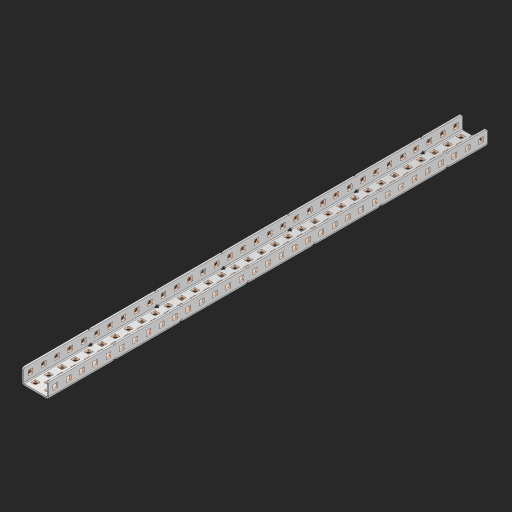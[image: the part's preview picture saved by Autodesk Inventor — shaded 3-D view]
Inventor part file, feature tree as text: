
AUTODESK INVENTOR PART (.ipt)
format: ipt  version: 2023 (Build 270158000, 158)  size: 2,024,960 bytes
history: native  units: in
note: dims shown in document units (in); Inventor stores cm internally (conversion verified against a paired STEP export)
features: other x172, extrude x163, sheet_metal_op x11, sketch x10, pattern_linear x2, mirror x1, chamfer x1
ambient origin geometry x8: Origin, YZ Plane, XZ Plane, XY Plane, X Axis, Y Axis, Z Axis, Center Point
bodies: Solid1 (feature_tree), Body (feature_tree)
feature tree (360):
  sheet_metal_op  "Flanges"
  other  "Flange Pattern Plane"
  other  "Flange Pattern Sketch"
  sheet_metal_op  "Flange Pattern"
  sheet_metal_op  "Body Pattern"
  pattern_linear  "Center Pattern"  Spacing1=0.0625in  [1 undecoded]
  other  "Arc Length"
  mirror  "Notch Mirror"
  pattern_linear  "Notch Pattern"  Spacing1=0.182in  [1 undecoded]
  chamfer  "End Chamfer"
  extrude  "Half Cut"  Depth=0.02in
  sketch  "Sketch1"  dims[d0=1.0in]
  other  "Plate1"
  sketch  "Sketch2"  dims[d1=16.5in]
  other  "Plate2"
  sheet_metal_op  "Bend1"
  sheet_metal_op  "Corner1"
  sketch  "Sketch3"  dims[d2=0.0625in]
  sketch  "Sketch7"  dims[d3=0.0625in]
  other  "Srf1"
  other  "Srf2"
  sketch  "Sketch8"  dims[d4=0.0312in]
  sketch  "Sketch9"  dims[d5=0.125in]
  other  "Srf91"
  sheet_metal_op  "Body Pattern Sketch"
  other  "Srf92"
  sketch  "Sketch13"  dims[d6=0.0625in]
  sketch  "Sketch14"  dims[d7=0.5in d8=90.0deg d9=0.0312in]
  sketch  "Sketch15"  dims[d10=0.25in]
  sketch  "Sketch16"  dims[d11=0.0625in d12=0.0625in d16=0.182in d17=0.02in d18=0.0625in d19=0.0in d20=0.25in d21=0.25in d38=12.9921in d40=0.5in d41=0.7874in d43=1.0in d46=0.172in d47=1.0in d48=0.0in d49=0.182in d50=0.02in d51=0.25in d52=0.25in d53=0.0625in d54=0.0in d55=0.172in d56=1.0in d57=0.0in d58=0.25in d60=12.9921in d62=0.5in d63=0.7874in d65=0.5in d85=0.1473in d86=0.1782in d88=0.04in d89=0.0625in d90=0.0in d91=0.04in d92=0.0491in d95=2.5in d96=0.04in d97=0.25in d98=45.0deg d99=0.25in d100=0.5in d101=0.0in d102=2.497in d106=0.182in d107=0.02in d108=0.5in d109=0.5in d110=0.0625in d111=0.0in d112=0.172in d113=0.5in d114=0.0in d117=0.5in d118=0.5in d119=0.5in]
  other  "Srf786"
  other  "Srf823"
  other  "Srf824"
  other  "Srf825"
  other  "Srf826"
  other  "Srf827"
  other  "Srf828"
  other  "Srf829"
  other  "Srf856"
  other  "Srf857"
  other  "Srf858"
  other  "Srf859"
  other  "Srf860"
  other  "Srf861"
  other  "Srf862"
  other  "Srf889"
  other  "Srf890"
  other  "Srf891"
  other  "Srf892"
  other  "Srf893"
  other  "Srf894"
  other  "Srf895"
  other  "Srf896"
  other  "Srf922"
  other  "Srf923"
  other  "Srf924"
  other  "Srf925"
  other  "Srf926"
  other  "Srf959"
  other  "Srf960"
  other  "Srf961"
  other  "Srf962"
  other  "Srf963"
  other  "Srf996"
  other  "Srf997"
  other  "Srf998"
  other  "Srf999"
  other  "Srf1000"
  other  "Srf1143"
  other  "Srf1144"
  other  "Srf1145"
  other  "Srf1146"
  other  "Srf1147"
  other  "Srf1148"
  other  "Srf1149"
  other  "Srf1150"
  other  "Srf1151"
  other  "Srf1152"
  other  "Srf1153"
  other  "Srf1154"
  other  "Srf1155"
  other  "Srf1156"
  other  "Srf1157"
  other  "Srf1158"
  other  "Srf1159"
  other  "Srf1160"
  other  "Srf1161"
  other  "Srf1162"
  other  "Srf1163"
  other  "Srf1164"
  other  "Srf1165"
  other  "Srf1166"
  other  "Srf1167"
  other  "Srf1168"
  other  "Srf1169"
  other  "Srf1170"
  other  "Srf1171"
  other  "Srf1172"
  other  "Srf1173"
  other  "Srf1174"
  other  "Srf1175"
  other  "Srf1176"
  other  "Srf1177"
  other  "Srf1178"
  other  "Srf1179"
  other  "Srf1180"
  other  "Srf1181"
  other  "Srf1182"
  other  "Srf1183"
  other  "Srf1184"
  other  "Srf1185"
  other  "Srf1186"
  other  "Srf1187"
  other  "Srf1188"
  other  "Srf1189"
  other  "Srf1190"
  other  "Srf1191"
  other  "Srf1192"
  other  "Srf1193"
  other  "Srf1194"
  other  "Srf1199"
  other  "Srf1200"
  other  "Srf1201"
  other  "Srf1202"
  other  "Srf1203"
  other  "Srf1204"
  other  "Srf1205"
  other  "Srf1206"
  other  "Srf1207"
  other  "Srf1208"
  other  "Srf1209"
  other  "Srf1210"
  other  "Srf1211"
  other  "Srf1212"
  other  "Srf1213"
  other  "Srf1214"
  other  "Srf1215"
  other  "Srf1216"
  other  "Srf1217"
  other  "Srf1218"
  other  "Srf1219"
  other  "Srf1220"
  other  "Srf1221"
  other  "Srf1222"
  other  "Srf1223"
  other  "Srf1224"
  other  "Srf1225"
  other  "Srf1226"
  other  "Srf1227"
  other  "Srf1228"
  other  "Srf1229"
  other  "Srf1230"
  other  "Srf1231"
  other  "Srf1232"
  other  "Srf1233"
  other  "Srf1234"
  other  "Srf1235"
  other  "Srf1236"
  other  "Srf1237"
  other  "Srf1238"
  other  "Srf1239"
  other  "Srf1240"
  other  "Srf1241"
  other  "Srf1242"
  other  "Srf1243"
  other  "Srf1244"
  other  "Srf1245"
  other  "Srf1246"
  other  "Srf1247"
  other  "Srf1248"
  other  "Srf1249"
  other  "Srf1250"
  other  "Srf1255"
  other  "Srf1256"
  other  "Srf1257"
  other  "Srf1258"
  other  "Srf1259"
  other  "Srf1260"
  other  "Srf1261"
  other  "Srf1262"
  other  "Srf1263"
  other  "Srf1264"
  other  "Srf1265"
  other  "Srf1266"
  other  "Srf1267"
  other  "Srf1268"
  other  "Srf1269"
  other  "Srf1270"
  other  "Srf1271"
  other  "Srf1272"
  other  "Srf1273"
  sheet_metal_op  "Flange Stamp"
  sheet_metal_op  "Flange Circle"
  sheet_metal_op  "Body Stamp"
  sheet_metal_op  "Body Circle"
  other  "Center Stamp"
  other  "Center Circle"
  sheet_metal_op  "Notch"
  extrude  "ExtrusionSrf2"  Depth=0.0625in
  extrude  "ExtrusionSrf92"  TaperAngle=0.0deg  [1 undecoded]
  extrude  "ExtrusionSrf823"  Depth=0.5in
  extrude  "ExtrusionSrf824"  Depth=0.5in
  extrude  "ExtrusionSrf825"  Depth=0.5in
  extrude  "ExtrusionSrf826"  Depth=0.5in
  extrude  "ExtrusionSrf827"  Depth=1.0in TaperAngle=0.0deg
  extrude  "ExtrusionSrf828"  Depth=0.5in
  extrude  "ExtrusionSrf829"  Depth=0.02in
  extrude  "ExtrusionSrf856"  Depth=0.5in
  extrude  "ExtrusionSrf857"  Depth=0.5in
  extrude  "ExtrusionSrf858"  Depth=0.0625in
  extrude  "ExtrusionSrf859"  TaperAngle=0.0deg  [1 undecoded]
  extrude  "ExtrusionSrf860"  Depth=0.5in
  extrude  "ExtrusionSrf861"  Depth=1.0in TaperAngle=0.0deg
  extrude  "ExtrusionSrf862"  Depth=0.5in
  extrude  "ExtrusionSrf889"  Depth=0.5in
  extrude  "ExtrusionSrf890"  Depth=0.5in
  extrude  "ExtrusionSrf891"  Depth=0.5in
  extrude  "ExtrusionSrf892"  Depth=0.5in
  extrude  "ExtrusionSrf893"  Depth=0.5in
  extrude  "ExtrusionSrf894"  Depth=0.0625in
  extrude  "ExtrusionSrf895"  TaperAngle=0.0deg  [1 undecoded]
  extrude  "ExtrusionSrf896"  Depth=0.5in
  extrude  "ExtrusionSrf922"  Depth=0.5in
  extrude  "ExtrusionSrf923"  Depth=2.5in
  extrude  "ExtrusionSrf924"  Depth=0.5in TaperAngle=45.0deg
  extrude  "ExtrusionSrf925"  Depth=0.5in
  extrude  "ExtrusionSrf926"  Depth=0.5in TaperAngle=0.0deg
  extrude  "ExtrusionSrf959"  Depth=0.5in
  extrude  "ExtrusionSrf960"  Depth=0.5in
  extrude  "ExtrusionSrf961"  Depth=0.02in
  extrude  "ExtrusionSrf962"  Depth=0.5in
  extrude  "ExtrusionSrf963"  Depth=0.5in
  extrude  "ExtrusionSrf996"  Depth=0.0625in
  extrude  "ExtrusionSrf997"  TaperAngle=0.0deg  [1 undecoded]
  extrude  "ExtrusionSrf998"  Depth=0.5in
  extrude  "ExtrusionSrf999"  Depth=0.5in TaperAngle=0.0deg
  extrude  "ExtrusionSrf1000"  Depth=0.5in
  extrude  "ExtrusionSrf1143"  Depth=0.5in
  extrude  "ExtrusionSrf1144"  Depth=0.5in
  extrude  "ExtrusionSrf1145"  [1 undecoded]
  extrude  "ExtrusionSrf1146"  [1 undecoded]
  extrude  "ExtrusionSrf1147"  [1 undecoded]
  extrude  "ExtrusionSrf1148"  [1 undecoded]
  extrude  "ExtrusionSrf1149"  [1 undecoded]
  extrude  "ExtrusionSrf1150"  [1 undecoded]
  extrude  "ExtrusionSrf1151"  [1 undecoded]
  extrude  "ExtrusionSrf1152"  [1 undecoded]
  extrude  "ExtrusionSrf1153"  [1 undecoded]
  extrude  "ExtrusionSrf1154"  [1 undecoded]
  extrude  "ExtrusionSrf1155"  [1 undecoded]
  extrude  "ExtrusionSrf1156"  [1 undecoded]
  extrude  "ExtrusionSrf1157"  [1 undecoded]
  extrude  "ExtrusionSrf1158"  [1 undecoded]
  extrude  "ExtrusionSrf1159"  [1 undecoded]
  extrude  "ExtrusionSrf1160"  [1 undecoded]
  extrude  "ExtrusionSrf1161"  [1 undecoded]
  extrude  "ExtrusionSrf1162"  [1 undecoded]
  extrude  "ExtrusionSrf1163"  [1 undecoded]
  extrude  "ExtrusionSrf1164"  [1 undecoded]
  extrude  "ExtrusionSrf1165"  [1 undecoded]
  extrude  "ExtrusionSrf1166"  [1 undecoded]
  extrude  "ExtrusionSrf1167"  [1 undecoded]
  extrude  "ExtrusionSrf1168"  [1 undecoded]
  extrude  "ExtrusionSrf1169"  [1 undecoded]
  extrude  "ExtrusionSrf1170"  [1 undecoded]
  extrude  "ExtrusionSrf1171"  [1 undecoded]
  extrude  "ExtrusionSrf1172"  [1 undecoded]
  extrude  "ExtrusionSrf1173"  [1 undecoded]
  extrude  "ExtrusionSrf1174"  [1 undecoded]
  extrude  "ExtrusionSrf1175"  [1 undecoded]
  extrude  "ExtrusionSrf1176"  [1 undecoded]
  extrude  "ExtrusionSrf1177"  [1 undecoded]
  extrude  "ExtrusionSrf1178"  [1 undecoded]
  extrude  "ExtrusionSrf1179"  [1 undecoded]
  extrude  "ExtrusionSrf1180"  [1 undecoded]
  extrude  "ExtrusionSrf1181"  [1 undecoded]
  extrude  "ExtrusionSrf1182"  [1 undecoded]
  extrude  "ExtrusionSrf1183"  [1 undecoded]
  extrude  "ExtrusionSrf1184"  [1 undecoded]
  extrude  "ExtrusionSrf1185"  [1 undecoded]
  extrude  "ExtrusionSrf1186"  [1 undecoded]
  extrude  "ExtrusionSrf1187"  [1 undecoded]
  extrude  "ExtrusionSrf1188"  [1 undecoded]
  extrude  "ExtrusionSrf1189"  [1 undecoded]
  extrude  "ExtrusionSrf1190"  [1 undecoded]
  extrude  "ExtrusionSrf1191"  [1 undecoded]
  extrude  "ExtrusionSrf1192"  [1 undecoded]
  extrude  "ExtrusionSrf1193"  [1 undecoded]
  extrude  "ExtrusionSrf1194"  [1 undecoded]
  extrude  "ExtrusionSrf1199"  [1 undecoded]
  extrude  "ExtrusionSrf1200"  [1 undecoded]
  extrude  "ExtrusionSrf1201"  [1 undecoded]
  extrude  "ExtrusionSrf1202"  [1 undecoded]
  extrude  "ExtrusionSrf1203"  [1 undecoded]
  extrude  "ExtrusionSrf1204"  [1 undecoded]
  extrude  "ExtrusionSrf1205"  [1 undecoded]
  extrude  "ExtrusionSrf1206"  [1 undecoded]
  extrude  "ExtrusionSrf1207"  [1 undecoded]
  extrude  "ExtrusionSrf1208"  [1 undecoded]
  extrude  "ExtrusionSrf1209"  [1 undecoded]
  extrude  "ExtrusionSrf1210"  [1 undecoded]
  extrude  "ExtrusionSrf1211"  [1 undecoded]
  extrude  "ExtrusionSrf1212"  [1 undecoded]
  extrude  "ExtrusionSrf1213"  [1 undecoded]
  extrude  "ExtrusionSrf1214"  [1 undecoded]
  extrude  "ExtrusionSrf1215"  [1 undecoded]
  extrude  "ExtrusionSrf1216"  [1 undecoded]
  extrude  "ExtrusionSrf1217"  [1 undecoded]
  extrude  "ExtrusionSrf1218"  [1 undecoded]
  extrude  "ExtrusionSrf1219"  [1 undecoded]
  extrude  "ExtrusionSrf1220"  [1 undecoded]
  extrude  "ExtrusionSrf1221"  [1 undecoded]
  extrude  "ExtrusionSrf1222"  [1 undecoded]
  extrude  "ExtrusionSrf1223"  [1 undecoded]
  extrude  "ExtrusionSrf1224"  [1 undecoded]
  extrude  "ExtrusionSrf1225"  [1 undecoded]
  extrude  "ExtrusionSrf1226"  [1 undecoded]
  extrude  "ExtrusionSrf1227"  [1 undecoded]
  extrude  "ExtrusionSrf1228"  [1 undecoded]
  extrude  "ExtrusionSrf1229"  [1 undecoded]
  extrude  "ExtrusionSrf1230"  [1 undecoded]
  extrude  "ExtrusionSrf1231"  [1 undecoded]
  extrude  "ExtrusionSrf1232"  [1 undecoded]
  extrude  "ExtrusionSrf1233"  [1 undecoded]
  extrude  "ExtrusionSrf1234"  [1 undecoded]
  extrude  "ExtrusionSrf1235"  [1 undecoded]
  extrude  "ExtrusionSrf1236"  [1 undecoded]
  extrude  "ExtrusionSrf1237"  [1 undecoded]
  extrude  "ExtrusionSrf1238"  [1 undecoded]
  extrude  "ExtrusionSrf1239"  [1 undecoded]
  extrude  "ExtrusionSrf1240"  [1 undecoded]
  extrude  "ExtrusionSrf1241"  [1 undecoded]
  extrude  "ExtrusionSrf1242"  [1 undecoded]
  extrude  "ExtrusionSrf1243"  [1 undecoded]
  extrude  "ExtrusionSrf1244"  [1 undecoded]
  extrude  "ExtrusionSrf1245"  [1 undecoded]
  extrude  "ExtrusionSrf1246"  [1 undecoded]
  extrude  "ExtrusionSrf1247"  [1 undecoded]
  extrude  "ExtrusionSrf1248"  [1 undecoded]
  extrude  "ExtrusionSrf1249"  [1 undecoded]
  extrude  "ExtrusionSrf1250"  [1 undecoded]
  extrude  "ExtrusionSrf1255"  [1 undecoded]
  extrude  "ExtrusionSrf1256"  [1 undecoded]
  extrude  "ExtrusionSrf1257"  [1 undecoded]
  extrude  "ExtrusionSrf1258"  [1 undecoded]
  extrude  "ExtrusionSrf1259"  [1 undecoded]
  extrude  "ExtrusionSrf1260"  [1 undecoded]
  extrude  "ExtrusionSrf1261"  [1 undecoded]
  extrude  "ExtrusionSrf1262"  [1 undecoded]
  extrude  "ExtrusionSrf1263"  [1 undecoded]
  extrude  "ExtrusionSrf1264"  [1 undecoded]
  extrude  "ExtrusionSrf1265"  [1 undecoded]
  extrude  "ExtrusionSrf1266"  [1 undecoded]
  extrude  "ExtrusionSrf1267"  [1 undecoded]
  extrude  "ExtrusionSrf1268"  [1 undecoded]
  extrude  "ExtrusionSrf1269"  [1 undecoded]
  extrude  "ExtrusionSrf1270"  [1 undecoded]
  extrude  "ExtrusionSrf1271"  [1 undecoded]
  extrude  "ExtrusionSrf1272"  [1 undecoded]
  extrude  "ExtrusionSrf1273"  [1 undecoded]
note: 127 required parameter values undecoded (feature->parameter linkage not recoverable at this tier; creation-order binding heuristic only, values carry confidence <= 0.55)
